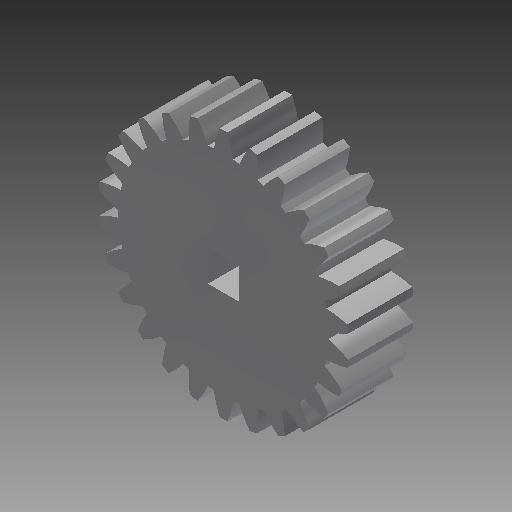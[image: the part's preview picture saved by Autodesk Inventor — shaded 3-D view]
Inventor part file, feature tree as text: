
AUTODESK INVENTOR PART (.ipt)
format: ipt  version: 2017 (Build 210142000, 142)  size: 257,024 bytes
history: native  units: mm (DEFAULTED — no unit token found)
features: plane x3, other x3, sketch x3, extrude x2
ambient origin geometry x8: Origin, YZ Plane, XZ Plane, XY Plane, X Axis, Y Axis, Z Axis, Center Point
bodies: Solid1 (feature_tree)
feature tree (11):
  extrude  "Extrusion1"  Depth=20.0mm TaperAngle=0.0deg
  plane  "Work Plane2"
  plane  "Work Plane8"
  plane  "Work Plane9"
  other  "Spur Gear"
  extrude  "Extrusion2"  Depth=10.0mm TaperAngle=0.0deg
  sketch  "Sketch1"  dims[d0=76.994148mm d1=20.0mm d2=0.0mm]
  sketch  "Sketch2"  dims[d3=71.724138mm d4=10.0mm d5=0.0mm]
  other  "Srf1"
  sketch  "Sketch3"  dims[d16=80.0mm d17=0.0mm d34=1.208305mm d39=0.0mm d41=0.0mm d43=80.0mm d46=80.0mm d47=0.0mm d48=0.0mm d49=9.525mm d50=10.0mm d51=0.0mm]
  other  "Pitch Diameter"
